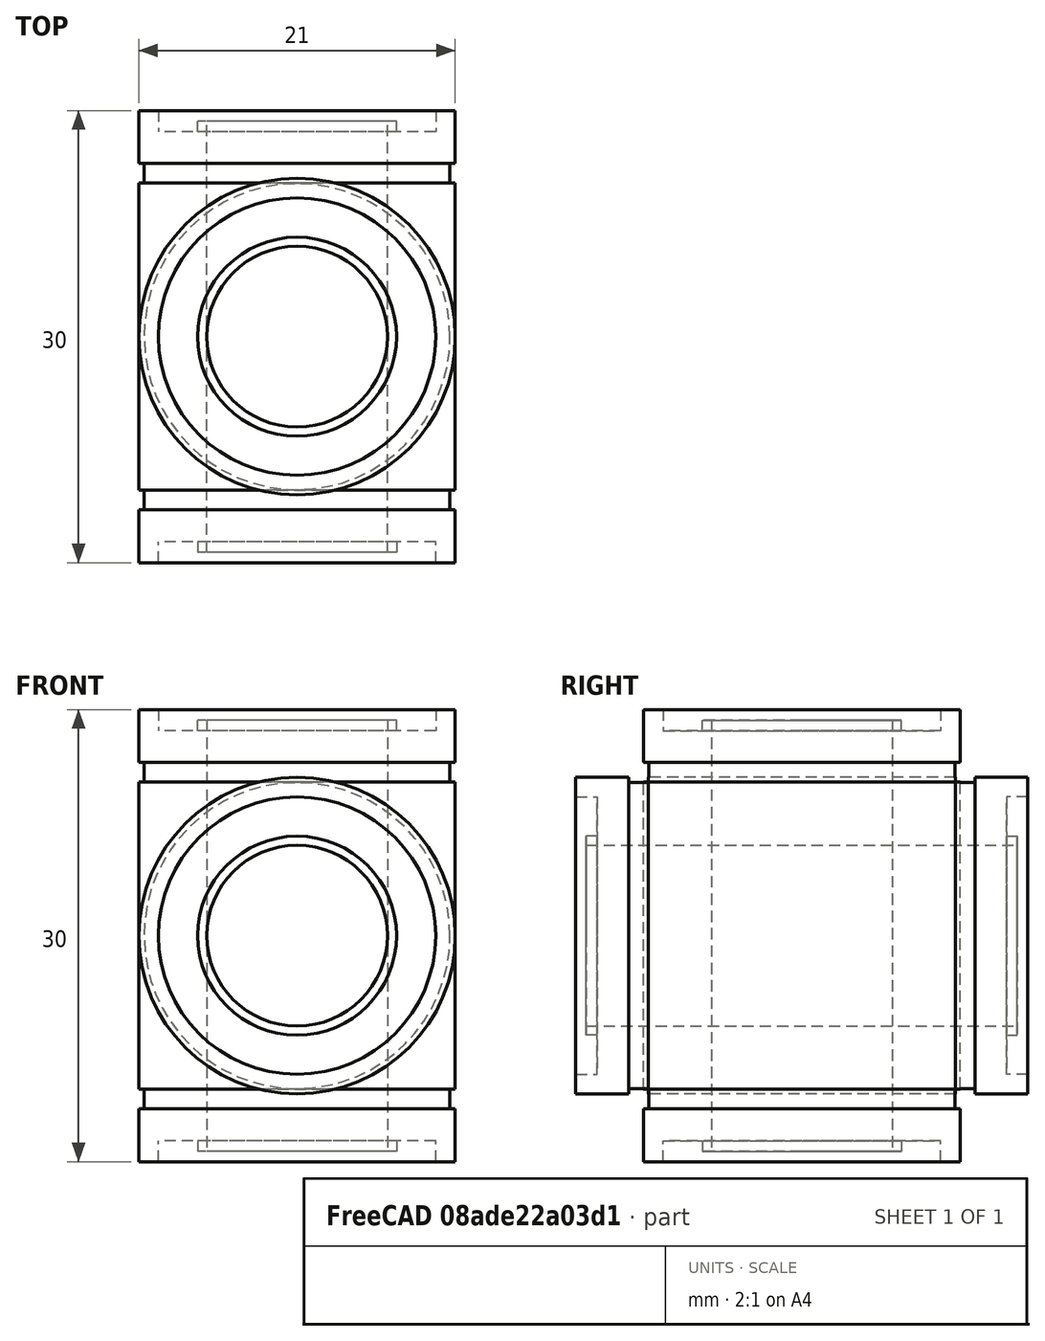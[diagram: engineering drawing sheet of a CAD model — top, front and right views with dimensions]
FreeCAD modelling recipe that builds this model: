
FCSTD DOCUMENT  (FreeCAD 0.15R4527 (Git))
Label: LM12uu
License: CC-BY 3.0
LicenseURL: http://creativecommons.org/licenses/by/3.0/
objects: Sketcher::SketchObject×1, PartDesign::Revolution×1, Part::Feature×1
note: 4 computed .brp shape members not serialized (recipe doc carries the construction recipe); baked Part::Feature solids carry a one-line shape summary decoded from their .brp

FEATURE [Sketcher::SketchObject] Sketch  label="lm12uu-cross-section"
  Placement = pos=(0,0,0) rot=(1,0,0;1.5708rad)
  sketch-geometry (20):
    g0: LineSegment StartX=10.5 StartY=-15 StartZ=0 EndX=10.5 EndY=-11.5 EndZ=0
    g1: LineSegment StartX=10.5 StartY=10.2 StartZ=0 EndX=10.15 EndY=10.2 EndZ=0
    g2: LineSegment StartX=10.15 StartY=10.2 StartZ=0 EndX=10.15 EndY=11.5 EndZ=0
    g3: LineSegment StartX=10.15 StartY=11.5 StartZ=0 EndX=10.5 EndY=11.5 EndZ=0
    g4: LineSegment StartX=10.5 StartY=11.5 StartZ=0 EndX=10.5 EndY=15 EndZ=0
    g5: LineSegment StartX=10.5 StartY=15 StartZ=0 EndX=9.2 EndY=15 EndZ=0
    g6: LineSegment StartX=9.2 StartY=15 StartZ=0 EndX=9.2 EndY=13.6 EndZ=0
    g7: LineSegment StartX=9.2 StartY=13.6 StartZ=0 EndX=6.6 EndY=13.6 EndZ=0
    g8: LineSegment StartX=6.6 StartY=13.6 StartZ=0 EndX=6.6 EndY=14.3 EndZ=0
    g9: LineSegment StartX=6.6 StartY=14.3 StartZ=0 EndX=6 EndY=14.3 EndZ=0
    g10: LineSegment StartX=6 StartY=14.3 StartZ=0 EndX=6 EndY=-14.3 EndZ=0
    g11: LineSegment StartX=10.5 StartY=-10.2 StartZ=0 EndX=10.15 EndY=-10.2 EndZ=0
    g12: LineSegment StartX=10.15 StartY=-11.5 StartZ=0 EndX=10.5 EndY=-11.5 EndZ=0
    g13: LineSegment StartX=10.5 StartY=-10.2 StartZ=0 EndX=10.5 EndY=10.2 EndZ=0
    g14: LineSegment StartX=10.15 StartY=-10.2 StartZ=0 EndX=10.15 EndY=-11.5 EndZ=0
    g15: LineSegment StartX=10.5 StartY=-15 StartZ=0 EndX=9.2 EndY=-15 EndZ=0
    g16: LineSegment StartX=9.2 StartY=-15 StartZ=0 EndX=9.2 EndY=-13.6 EndZ=0
    g17: LineSegment StartX=9.2 StartY=-13.6 StartZ=0 EndX=6.6 EndY=-13.6 EndZ=0
    g18: LineSegment StartX=6.6 StartY=-13.6 StartZ=0 EndX=6.6 EndY=-14.3 EndZ=0
    g19: LineSegment StartX=6.6 StartY=-14.3 StartZ=0 EndX=6 EndY=-14.3 EndZ=0
  constraints (58):
    c: Coincident(g13,g1)
    c: Coincident(g1,g2)
    c: Vertical(g2)
    c: Coincident(g2,g3)
    c: Coincident(g3,g4)
    c: Vertical(g4)
    c: Coincident(g4,g5)
    c: Coincident(g5,g6)
    c: Vertical(g6)
    c: Coincident(g6,g7)
    c: Horizontal(g7)
    c: Coincident(g7,g8)
    c: Vertical(g8)
    c: Coincident(g8,g9)
    c: Horizontal(g9)
    c: Coincident(g9,g10)
    c: Vertical(g10)
    c: Horizontal(g1)
    c: Horizontal(g5)
    c: Horizontal(g3)
    c: PointOnObject(g3,g0)
    c: Symmetric(g0,g4,g-1)
    c: DistanceY(g4,g0) = -30
    c: DistanceY(g2) = 1.3
    c: DistanceX(g3) = 0.35
    c: DistanceX(g-1,g4) = 10.5
    c: DistanceX(g-1,g9) = 6
    c: DistanceX(g5) = -1.3
    c: DistanceX(g9) = -0.6
    c: DistanceY(g6) = -1.4
    c: DistanceY(g8) = 0.7
    c: Horizontal(g11)
    c: Horizontal(g12)
    c: Coincident(g13,g11)
    c: Tangent(g0,g13)
    c: Coincident(g12,g0)
    c: PointOnObject(g14,g11)
    c: Coincident(g14,g12)
    c: Vertical(g14)
    c: Symmetric(g1,g11,g-1)
    c: DistanceY(g13) = 20.4
    c: Equal(g14,g2)
    c: Coincident(g0,g15)
    c: Horizontal(g15)
    c: Coincident(g15,g16)
    c: Vertical(g16)
    c: Coincident(g16,g17)
    c: Horizontal(g17)
    c: Coincident(g17,g18)
    c: Vertical(g18)
    c: Coincident(g18,g19)
    c: Horizontal(g19)
    c: Coincident(g10,g19)
    c: Symmetric(g10,g9,g-1)
    c: Symmetric(g16,g6,g-1)
    c: Symmetric(g17,g7,g-1)
    c: Coincident(g14,g11)
    c: PointOnObject(g11,g2)
FEATURE [PartDesign::Revolution] Revolution  label="LM12uu"
  Angle = 360
  Axis = (0,0,1)
  Base = (0,0,0)
  Placement = pos=(0,0,0) rot=(1,0,0;1.5708rad)
  ReferenceAxis = -> Sketch [V_Axis]
  Reversed = true
  Sketch = -> Sketch
FEATURE [Part::Feature] Revolution001  label="LM12uu001"
  Placement = pos=(0,0,0) rot=(1,0,0;1.5708rad)
  shape: bbox 21 x 30 x 21 mm, 20 faces (baked)
